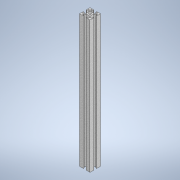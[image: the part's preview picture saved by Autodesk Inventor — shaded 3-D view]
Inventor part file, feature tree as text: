
AUTODESK INVENTOR PART (.ipt)
format: ipt  version: 2022 (Build 260153000, 153)  size: 220,160 bytes
history: native  units: in
note: dims shown in document units (in); Inventor stores cm internally (conversion verified against a paired STEP export)
features: direct_edit x1, extrude x1, sketch x1, projected_geometry x1, move_body x1
ambient origin geometry x8: Origin, YZ Plane, XZ Plane, XY Plane, X Axis, Y Axis, Z Axis, Center Point
bodies: Body1 (feature_tree)
feature tree (5):
  direct_edit  "Direct Edit1"
  extrude  "Extrusion1"  Depth=9.8425in TaperAngle=0.0deg
  sketch  "Sketch1"  dims[d0=0.0in d1=0.0in d2=-0.0394in d3=9.8425in d4=0.0in]
  projected_geometry  "Projected Loop1"
  move_body  "Move1"
